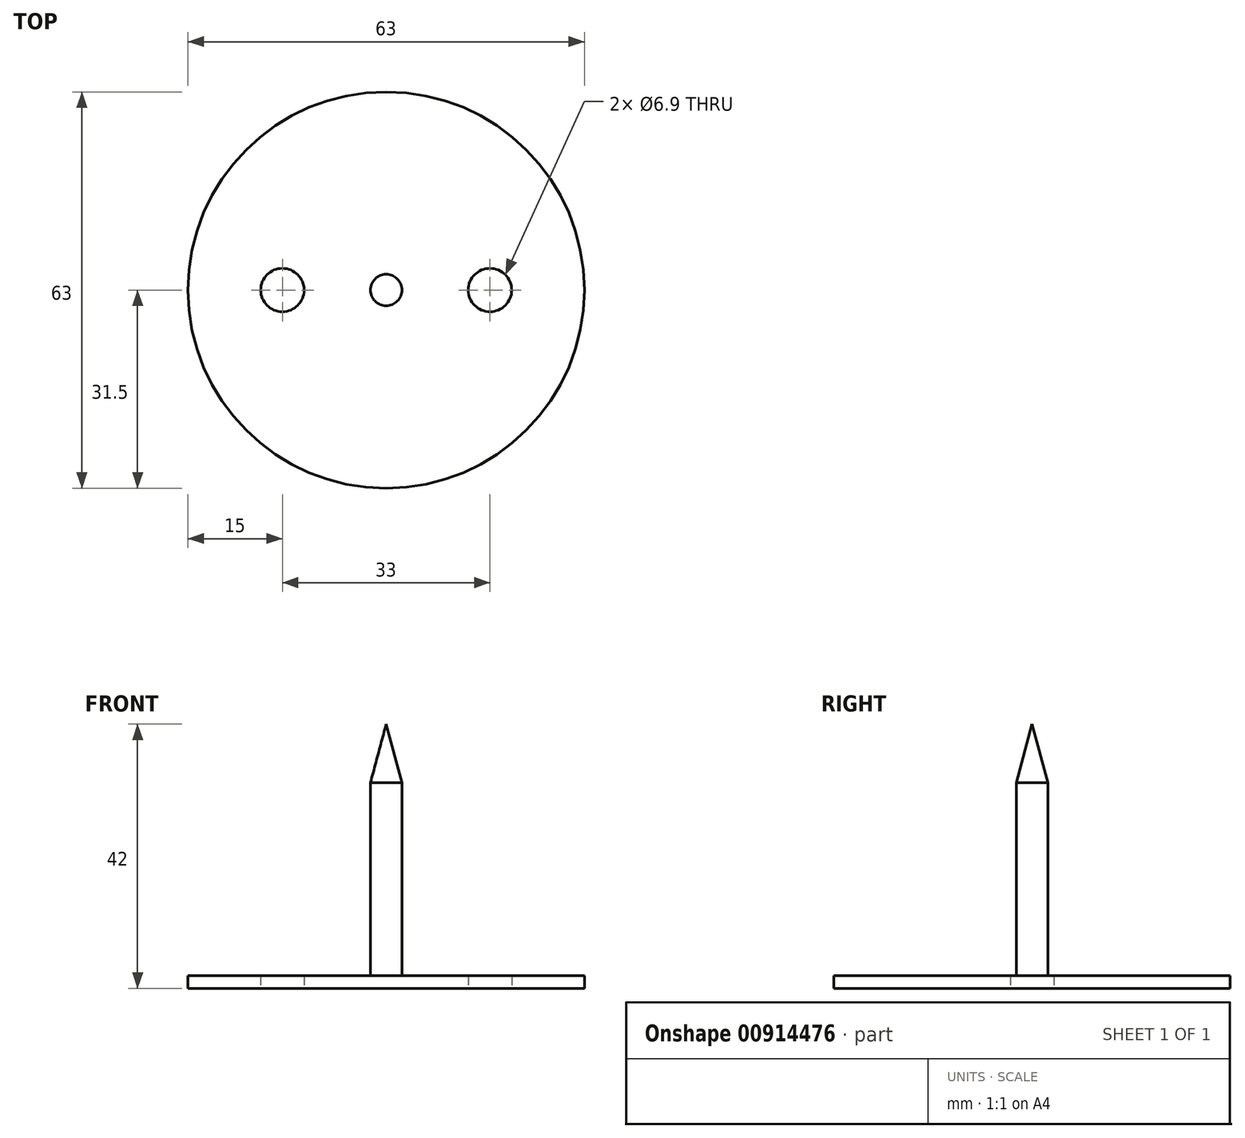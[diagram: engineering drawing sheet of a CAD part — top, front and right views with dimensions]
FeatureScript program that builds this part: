
annotation { "Feature Type Name" : "Feature", "Feature Type Description" : "" }
export const myFeature = defineFeature(function(context is Context, id is Id, definition is map)
    precondition{}
    {
        {
            var Q0;
            Q0=qCreatedBy(makeId("Top.planeOp"),FACE);
            var sketch = newSketch(context, id + "F0", { "sketchPlane" : qUnion([Q0])});
            skCircle(sketch, "E0", {"center": v(0, 0) * mm, "radius": 31.5 * mm});
            skCircle(sketch, "E1", {"center": v(-16.5, 0) * mm, "radius": 3.45 * mm});
            skCircle(sketch, "E2", {"center": v(16.5, 0) * mm, "radius": 3.45 * mm});
            skSolve(sketch);
        }
        {
            var Q0;
            Q0 = qSketchRegion(id + "F0", true);
            extrude(context, id + "F1", {"entities" : qUnion([Q0]), "depth" : 2 * mm, "offsetDistance" : 25 * mm});
        }
        {
            var Q0;
            Q0=makeQuery(id+"F1.opExtrude","CAP_FACE",FACE,{"disambiguationData":[OSD([sQuery(id+"F0.wireOp",EDGE,"E0"),sQuery(id+"F0.wireOp",EDGE,"E1"),sQuery(id+"F0.wireOp",EDGE,"E2")])],"isStart":false});
            var sketch = newSketch(context, id + "F2", { "sketchPlane" : qUnion([Q0])});
            skCircle(sketch, "E3", {"center": v(0, 0) * mm, "radius": 2.5 * mm});
            skSolve(sketch);
        }
        {
            var Q0;
            Q0 = qSketchRegion(id + "F2", true);
            extrude(context, id + "F3", {"entities" : qUnion([Q0]), "operationType" : NewBodyOperationType.ADD, "depth" : 40 * mm, "offsetDistance" : 25 * mm});
        }
        {
            var Q0;
            Q0=makeQuery(id+"F3.opExtrude","CAP_EDGE",EDGE,{"disambiguationData":[OSD([sQuery(id+"F2.wireOp",EDGE,"E3")])],"isStart":false});
            chamfer(context, id + "F4", {"entities" : qUnion([Q0]), "chamferType" : ChamferType.OFFSET_ANGLE, "width" : 2.5 * mm, "oppositeDirection" : false, "angle" : 75 * degree, "tangentPropagation" : true});
        }
    });
